# Revit family: xxxxxxxThermostatic_Mixing_Valve-WATTS-LFMMV_Series
name_source: partatom
category: Pipe Accessories
units: mm (PartAtom-declared; Revit-internal decimal feet)

## family parameters
Always vertical = No
Cut with Voids When Loaded = No
OmniClass Number = 23.65.55.14.24
OmniClass Title = Mixing Valves for Liquid Services
Part Type = Valve - Normal
Round Connector Dimension = Use Diameter
Shared = Yes
Work Plane-Based = No

## types (17) — shared parameters
Assembly Code = D2090900
CW Connection = Yes
Country = United States
Description = Lead Free* Thermostatic Mixing Valves
Finish = Cast Copper-WATTS-Lead Free-Silicon Alloy
Finish- Disc & Spring = Metal-WATTS-Stainless Steel
Finish- O-Rings = Rubber-WATTS-Ethylene Propylene Diene Monomer
Finish- Pistons = Plastic-WATTS-Polysulfone
Finish- Thermostat Assembly = Metal-WATTS-Copper
HW Connection = Yes
HW Inlet to Outlet Temperature Differential = 5°F (3°C) above set point
IAPMO Compliance = ASSE 1017 Certified, ASSE 1069 Certified, ASSE 1070 Certified, IAPMO cUPC Certified and approved to CSA B125.3 and, CSA B125.70, NSF/ANSI/CAN 61 & NSF/ANSI/CAN 372 Certified
Inlet Temperature = Hot Inlet, 120°F – 180°F (49°C – 82°C), Cold Inlet, 39°F – 85°F (4°C – 29°C)
Installation Instruction Link = https://www.watts.com
Manufacturer = WATTS
Manufacturer Product Line = Plumbing & Flow Control Solutions
Material = Cast Copper-WATTS-Lead Free-Silicon Alloy
Max. Hot Water Temp. = 200°F (93°C)
Max. Pressure (PSI) = 150
Maximum Flow Rate = 20 GPM
Maximum Pressure Differential between Hot & Cold Water Supplies = 25%
Minimum Flow Rate = 1 GPM
Minimum Supply Pressure (Static) = 30psi (207 kPa)
Optional Viega Pro-Press Connection = No
Product Documentation Link = https://www.watts.com
Product Page URL = https://www.watts.com
Region = North America
Revised Date = 05/09/2022
Temperature Out = Field range: 80°F – 120°F (27°C – 49°C), adjustable. Accurate within ±3°F (1.7°C)
Tempered Connection = Yes
URL = https://www.watts.com
Vent Connection = No
Waste Connection = No

## per-type parameters (varying)
| type | A | A/2 | B | C | Cold Water Connection Diameter | Connection CW Inlet Description | Connection HW Inlet Description | Connection Outlet Description | D | Hot Water Connection Diameter | Outlet/2 | Tempered Water Connection Diameter | Weight Lbs |
| LFMMVM1-UT - 0.5" | 4 7/8" | 2 7/16" | 5 7/16" | 3 3/16" | 1/2" | 1/2" Union Thread Cold Water Inlet | 1/2" Union Thread Hot Water Inlet | 1/2" Union Thread Tempered Water Outlet | 5/8" | 1/2" | 3/8" | 1/2" | 1.8 lbs (0.8 kg) |
| LFMMVM1-UT - 0.75" | 4 7/8" | 2 7/16" | 5 7/16" | 3 3/16" | 3/4" | 3/4" Union Thread Cold Water Inlet | 3/4" Union Thread Hot Water Inlet | 3/4" Union Thread Tempered Water Outlet | 5/8" | 3/4" | 1/2" | 3/4" | 2.4 lbs (1.1 kg) |
| LFMMVM1-UT - 1" | 5 5/16" | 2 21/32" | 5 5/8" | 3 3/8" | 1" | 1" Union Thread Cold Water Inlet | 1" Union Thread Hot Water Inlet | 1" Union Thread Tempered Water Outlet | 3/4" | 1" | 5/8" | 1" | 3.0 lbs (1.4 kg) |
| LFMMVM1-US - 0.5" | 4 13/16" | 2 13/32" | 5 3/8" | 3 1/8" | 1/2" | 1/2" Union Sweat Cold Water Inlet | 1/2" Union Sweat Hot Water Inlet | 1/2" Union Sweat Tempered Water Outlet | 5/8" | 1/2" | 3/8" | 1/2" | 1.7 lbs (0.8 kg) |
| LFMMVM1-US - 0.75" | 5 5/16" | 2 21/32" | 5 5/8" | 3 3/8" | 3/4" | 3/4" Union Sweat Cold Water Inlet | 3/4" Union Sweat Hot Water Inlet | 3/4" Union Sweat Tempered Water Outlet | 7/8" | 3/4" | 1/2" | 3/4" | 2.3 lbs (1.0 kg) |
| LFMMVM1-US - 1" | 5 13/16" | 2 29/32" | 5 7/8" | 3 5/8" | 3/4" | 1" Union Sweat Cold Water Inlet | 1" Union Sweat Hot Water Inlet | 1" Union Sweat Tempered Water Outlet | 1 1/8" | 3/4" | 1/2" | 3/4" | 2.9 lbs (1.3 kg) |
| LFMMVM1-PEX - 0.5" | 5 1/4" | 2 5/8" | 5 9/16" | 3 5/16" | 3/4" | 1/2" Union PEX Cold Water Inlet | 1/2" Union PEX Hot Water Inlet | 1/2" Union PEX Tempered Water Outlet | 13/16" | 3/4" | 1/2" | 3/4" | 1.8 lbs (0.8 kg) |
| LFMMVM1-PEX - 0.75" | 5 1/2" | 2 3/4" | 5 11/16" | 3 7/16" | 3/4" | 3/4" Union PEX Cold Water Inlet | 3/4" Union PEX Hot Water Inlet | 3/4" Union PEX Tempered Water Outlet | 15/16" | 3/4" | 1/2" | 3/4" | 2.5 lbs (1.1 kg) |
| LFMMVM1-PEX - 1" | 5 7/8" | 2 15/16" | 5 7/8" | 3 5/8" | 1" | 1" Union PEX Cold Water Inlet | 1" Union PEX Hot Water Inlet | 1" Union PEX Tempered Water Outlet | 1 1/8" | 1" | 5/8" | 1" | 3.1 lbs (1.4 kg) |
| LFMMVM1-CEF - 0.5" | 5 1/2" | 2 3/4" | 5 11/16" | 3 7/16" | 1/2" | 1/2" Union CEF Cold Water Inlet | 1/2" Union CEF Hot Water Inlet | 1/2" Union CEF Tempered Water Outlet | 7/8" | 1/2" | 3/8" | 1/2" | 1.8 lbs (0.8 kg) |
| LFMMVM1-CEF - 0.75" | 6 1/16" | 3 1/32" | 5 15/16" | 3 11/16" | 3/4" | 3/4" Union CEF Cold Water Inlet | 3/4" Union CEF Hot Water Inlet | 3/4" Union CEF Tempered Water Outlet | 3/16" | 3/4" | 1/2" | 3/4" | 2.4 lbs (1.1 kg) |
| LFMMVM1-CPVC - 0.5" | 4 3/4" | 2 3/8" | 5 5/16" | 3 1/16" | 1/2" | 1/2" Union CPVC Cold Water Inlet | 1/2" Union CPVC Hot Water Inlet | 1/2" Union CPVC Tempered Water Outlet | 9/16" | 1/2" | 3/8" | 1/2" | 1.6 lbs (0.7 kg) |
| LFMMVM1-CPVC - 0.75" | 5 1/4" | 2 5/8" | 5 9/16" | 3 5/16" | 3/4" | 3/4" Union CPVC Cold Water Inlet | 3/4" Union CPVC Hot Water Inlet | 3/4" Union CPVC Tempered Water Outlet | 13/16" | 3/4" | 1/2" | 3/4" | 2.2 lbs (1.0 kg) |
| LFMMVM1-CPVC - 1" | 5 11/16" | 2 27/32" | 5 13/16" | 3 9/16" | 1" | 1" Union CPVC Cold Water Inlet | 1" Union CPVC Hot Water Inlet | 1" Union CPVC Tempered Water Outlet | 1" | 1" | 5/8" | 1" | 2.6 lbs (1.2 kg) |
| LFMMVM1-QC - 0.5" | 6 5/8" | 3 5/16" | 6 1/4" | 4" | 1/2" | 1/2" Union Quick-Connect Cold Water Inlet | 1/2" Union Quick-Connect Hot Water Inlet | 1/2" Union Quick-Connect  Tempered Water Outlet | 1 1/2" | 1/2" | 3/8" | 1/2" | 2.1 lbs (0.9 kg) |
| LFMMVM1-QC - 0.75" | 6 15/16" | 3 15/32" | 6 7/16" | 4 3/16" | 3/4" | 3/4" Union Quick-Connect Cold Water Inlet | 3/4" Union Quick-Connect Hot Water Inlet | 3/4" Union Quick-Connect  Tempered Water Outlet | 1 11/16" | 3/4" | 1/2" | 3/4" | 2.8 lbs (1.3 kg) |
| LFMMVM1-QC - 1" | 7 1/8" | 3 9/16" | 6 1/2" | 4 1/4" | 1" | 1" Union Quick-Connect Cold Water Inlet | 1" Union Quick-Connect Hot Water Inlet | 1" Union Quick-Connect  Tempered Water Outlet | 1 3/4" | 1" | 5/8" | 1" | 3.5 lbs (1.6 kg) |

note: column(s) folded — value = type name in every type: Model

## geometry (parser evidence)
native form markers: Sweep x2
no freeform markers — native parametric forms only
